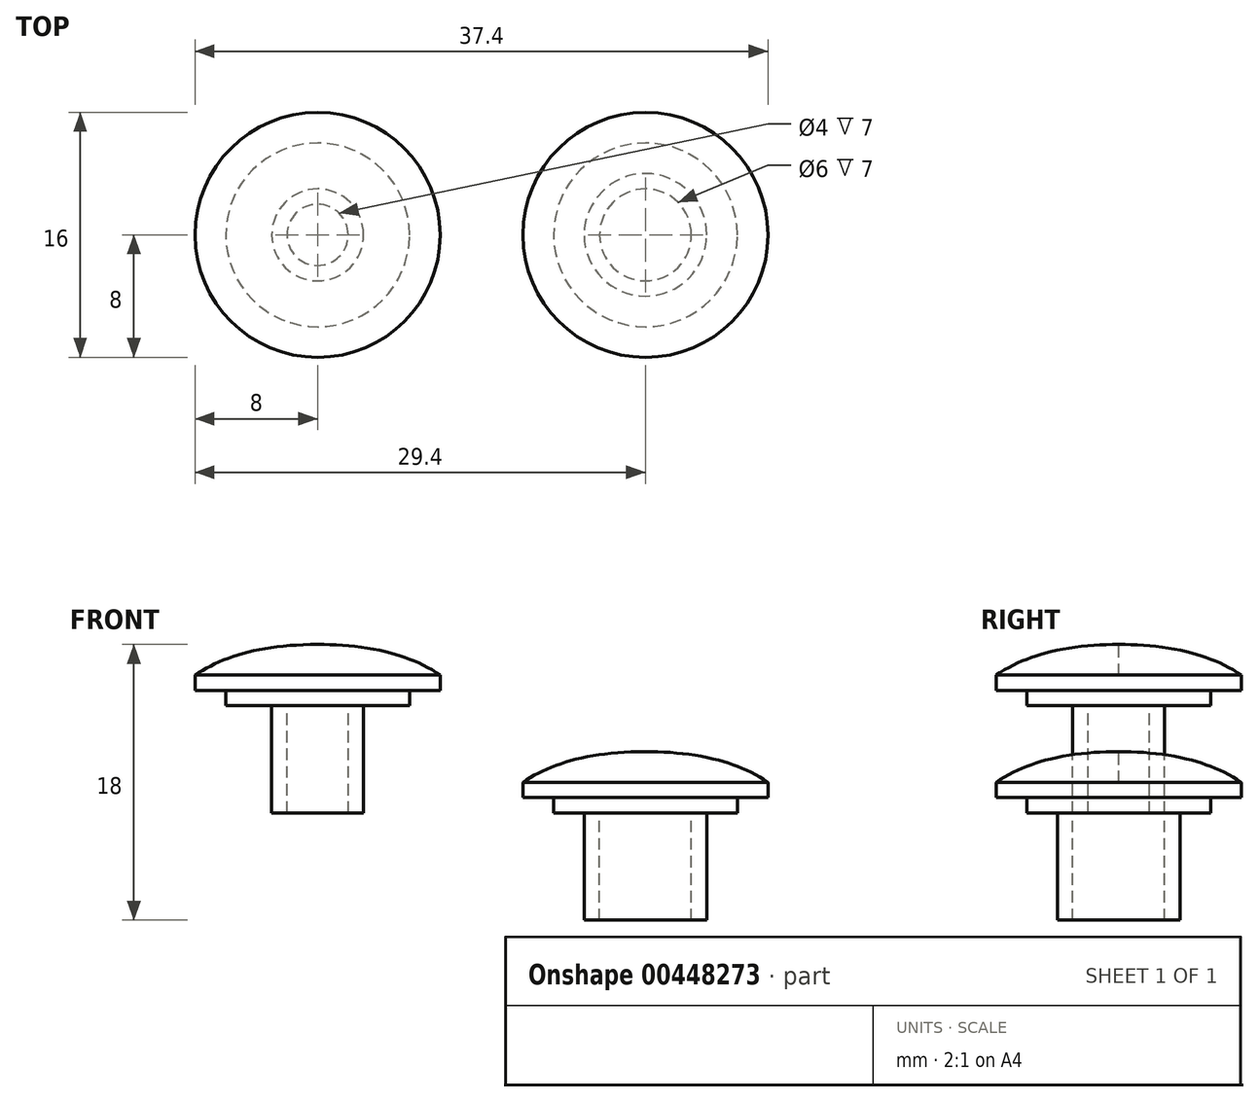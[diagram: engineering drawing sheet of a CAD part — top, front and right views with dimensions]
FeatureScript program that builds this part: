
annotation { "Feature Type Name" : "Feature", "Feature Type Description" : "" }
export const myFeature = defineFeature(function(context is Context, id is Id, definition is map)
    precondition{}
    {
        {
            var Q0;
            Q0=qCreatedBy(makeId("Front.planeOp"),FACE);
            var sketch = newSketch(context, id + "F0", { "sketchPlane" : qUnion([Q0])});
            skLineSegment(sketch, "E0", {"start": v(0, 4) * mm, "end": v(0, 0) * mm});
            skLineSegment(sketch, "E1", {"start": v(0, 0) * mm, "end": v(-3, 0) * mm});
            skLineSegment(sketch, "E2", {"start": v(-3, 0) * mm, "end": v(-3, -7) * mm});
            skLineSegment(sketch, "E3", {"start": v(-3, -7) * mm, "end": v(-4, -7) * mm});
            skLineSegment(sketch, "E4", {"start": v(-4, -7) * mm, "end": v(-4, 0) * mm});
            skLineSegment(sketch, "E5", {"start": v(-4, 0) * mm, "end": v(-6, 0) * mm});
            skLineSegment(sketch, "E6", {"start": v(-6, 0) * mm, "end": v(-6, 1) * mm});
            skLineSegment(sketch, "E7", {"start": v(-6, 1) * mm, "end": v(-8, 1) * mm});
            skLineSegment(sketch, "E8", {"start": v(-8, 1) * mm, "end": v(-8, 2) * mm});
            skFitSpline(sketch, "E9", {"points": [v(-8, 2) * mm, v(0, 4) * mm], "startDerivative": vector(5.4, 3.68) * mm, "endDerivative": vector(11.02, 0) * mm});
            skSolve(sketch);
        }
        {
            var Q0;
            Q0=makeQuery(id+"F0.imprint","IMPRINT",FACE,{"disambiguationData":[TD([[makeQuery(id+"F0.imprint","IMPRINT",EDGE,{"derivedFrom":sQuery(id+"F0.wireOp",EDGE,"E0")}),-1.0]])]});
            var Q1;
            Q1=sQuery(id+"F0.wireOp",EDGE,"E0");
            revolve(context, id + "F1", {"entities" : qUnion([Q0]), "axis" : qUnion([Q1]), "revolveType" : RevolveType.FULL});
        }
        {
            var Q0;
            Q0=qCreatedBy(makeId("Front.planeOp"),FACE);
            var sketch = newSketch(context, id + "F2", { "sketchPlane" : qUnion([Q0])});
            skLineSegment(sketch, "E10", {"start": v(-21.4, 11) * mm, "end": v(-21.4, 7) * mm});
            skLineSegment(sketch, "E11", {"start": v(-21.4, 7) * mm, "end": v(-23.4, 7) * mm});
            skLineSegment(sketch, "E12", {"start": v(-23.4, 7) * mm, "end": v(-23.4, 0) * mm});
            skLineSegment(sketch, "E13", {"start": v(-23.4, 0) * mm, "end": v(-24.4, 0) * mm});
            skLineSegment(sketch, "E14", {"start": v(-24.4, 0) * mm, "end": v(-24.4, 7) * mm});
            skLineSegment(sketch, "E15", {"start": v(-24.4, 7) * mm, "end": v(-27.4, 7) * mm});
            skLineSegment(sketch, "E16", {"start": v(-27.4, 7) * mm, "end": v(-27.4, 8) * mm});
            skLineSegment(sketch, "E17", {"start": v(-27.4, 8) * mm, "end": v(-29.4, 8) * mm});
            skLineSegment(sketch, "E18", {"start": v(-29.4, 8) * mm, "end": v(-29.4, 9) * mm});
            skFitSpline(sketch, "E19", {"points": [v(-29.4, 9) * mm, v(-21.4, 11) * mm], "startDerivative": vector(5.4, 3.68) * mm, "endDerivative": vector(11.02, 0) * mm});
            skSolve(sketch);
        }
        {
            var Q0;
            Q0=makeQuery(id+"F2.imprint","IMPRINT",FACE,{"disambiguationData":[TD([[makeQuery(id+"F2.imprint","IMPRINT",EDGE,{"derivedFrom":sQuery(id+"F2.wireOp",EDGE,"E10")}),-1.0]])]});
            var Q1;
            Q1=sQuery(id+"F2.wireOp",EDGE,"E10");
            revolve(context, id + "F3", {"entities" : qUnion([Q0]), "axis" : qUnion([Q1]), "revolveType" : RevolveType.FULL});
        }
    });
